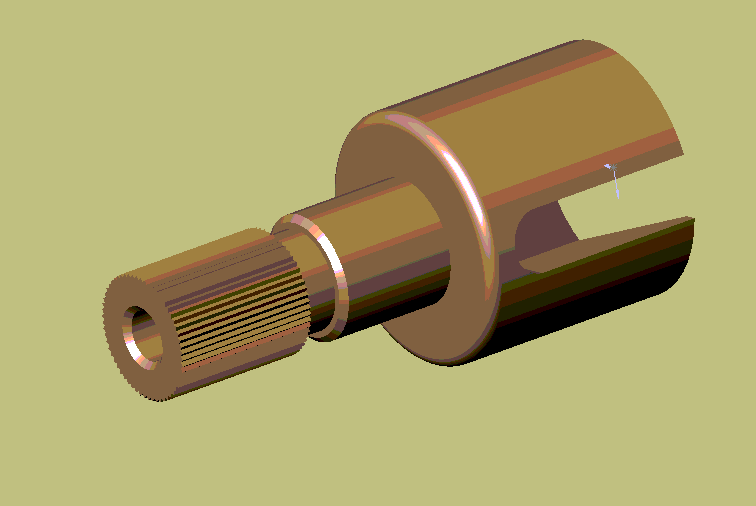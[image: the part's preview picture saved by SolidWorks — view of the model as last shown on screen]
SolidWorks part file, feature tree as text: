
SOLIDWORKS PART (.sldprt)
format: sldprt  version: not decoded by parser v0  size: 370,176 bytes
history: native  units: mm
features: sketch x8, plane x3, fillet x3, extrude x2, cut_extrude x2, material x1, cut_revolve x1, chamfer x1 + 1 further entry (+7 scaffold rows collapsed)
feature tree (29):
  scaffold x7  (default folders/planes/origin — collapsed)
  material  "Matériau <non spécifié>"
  "Corps de surface"
  plane  "Plane1"
  plane  "Plane2"
  plane  "Plane3"
  sketch  "Esquisse1"  dims[D1=10.0mm]
  extrude  "Base-Extrusion"  Depth=9.5mm
  sketch  "Esquisse2"  dims[D1=5.0mm]
  extrude  "Boss.-Extru.1"  Depth=5mm
  fillet  "Congé1"  Radius=0.5mm
  sketch  "Esquisse7"  dims[D1=7.0mm D2=2.5mm]
  cut_extrude  "Enlèv. mat.-Extru.1"  Depth=32mm
  sketch  "Esquisse8"  dims[D1=4.0mm D2=3.0mm D3=4.0mm D4=1.5mm D5=4.5mm]
  cut_revolve  "Enlèvement de matière-Révolution1"  Angle=360deg
  sketch  "Esquisse10"  dims[c1.D1=5.0mm c1.D4=4.75mm c1.D2=3.0mm c2.D2=6.0deg c2.D3=~4.123106mm c3.D3=3.0deg]
  sketch  "Esquisse11"  dims[D1=4.0mm]
  fillet  "Boss.-Extru.2"  Radius=1.5mm
  sketch  "Esquisse12"
  fillet  "Boss.-Extru.3"  Radius=6mm
  sketch  "Esquisse13"  dims[D1=2.0mm]
  cut_extrude  "Enlèv. mat.-Extru.2"  Depth=18mm
  chamfer  "Chanfrein1"  Distance=0.25mm Angle=45deg
decode coverage: 16 of 17 modeling features carry decoded parameters; 1 rows unclassified (native names shown)
note: ~ marks probable driven/reference dimensions
note: suppression state not decoded; provenance and decode notes live in map.json
